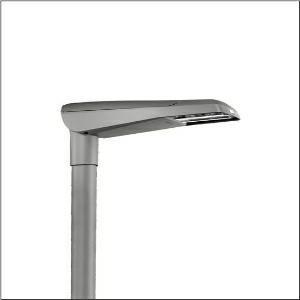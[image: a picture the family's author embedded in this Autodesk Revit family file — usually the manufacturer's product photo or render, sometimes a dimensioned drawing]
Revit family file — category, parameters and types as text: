
# Revit family: streetlight_sl_11_iq_micro___st0_5a_5xc1b41e08ce_6374
name_source: partatom
category: Lighting Fixtures
units: mm (PartAtom-declared; Revit-internal decimal feet)

## family parameters
Cut with Voids When Loaded = No
Host = Face
Light Source = No
Part Type = Normal
Room Calculation Point = No
Round Connector Dimension = Use Diameter
Shared = No

## types (1)
- --- (1 x LED, 1940 lm, 12.6 W, 4000K)
    Apparent Load = 13 VA
    CIE Flux Codes = 42 72 97 100 100
    Color Rendering = 70
    Color Temperature = 4000K
    Default Elevation = 1800 mm
    Description = Streetlight SL 11 iQ micro, mast luminaire, primary light control with 3 zone facetted reflector, of plastic, silver coated, highly specular, primary optical cover: cover, of PMMA, transparent, light distribution: ST0.5a, light emission: direct distribution, primary light characteristic: asymmetric, installation type: post-top, side-entry, lamps: LED, High Power LED, rated values: 1.940lm | 12,6W | 154lm/W (begin service life); end service life: 1.940lm | 12,9W; at 50% lumin. flux: 970lm | 6,8W | 142,6lm/W, colour temperature: 4000K, colour rendering: CRI > 70, light colour: 740, light setting 1 begin service life: 100% | 1.940lm | 12,6W | 154lm/W | 4.000K, light setting 1 end service life: 12,9W, further light settings possible, control: optimised constant luminous flux control (CLO 2.0), Desk-Remote (wireless, voltage-free reading and setting of iQ features in the workshop via application-optimized NFC function/RFID function), Light-Fading, Smart-Wire, Night-Set, Lumen-Switch, Temp-Guard, Auto-Match, with cable H07RN-F 3x 1.5mm², mains connection: 230..240V, AC, 50/60Hz, connection cable pre-assembled, cable length: 5,5m, luminaire housing, of diecast aluminium, powder-coated, SITECO metallic grey (DB 702S), please order mast flange separately, inclination adjustable without tools: 0°, 5°, 10°, 15° (post-top) | 0°, -5°, -10°, -15° (side-entry), sealing non-destructively replaceable, multi-level sealing system, length: 600mm, width: 174mm, height: 116mm, mast flange for spigot size: 42mm (side-entry): 5XC10008XM4, 60/48mm (side-entry/post-top): 5XC10108XM2, 76/60mm (side-entry/post-top): 5XC10108XM1, equipment: standard, protection rating (complete): IP66, insulation class (complete): insulation class II (safety insulation), certification: CE, ENEC, ENEC+, VDE, impact resistance: IK10, permissible operating ambient temperature for outdoor applications: -25..+50°C, standard-compliant lighting for roads and squares, Environmental Product Declaration (EPD) tested and certified by an independent institute, packaging unit: 1 piece

Light Distribution: ST0.5a
    Height = 116 mm
    Lamp = 1 x LED
    Lamp Light Flux = 1940 lm
    Lamp Power = 12.6 W
    Lamp count = 1
    Length = 600 mm
    Luminous efficacy = 154 lm/W
    Manufacturer = Siteco
    ModVariant = No
    Model = 5XC1B41E08CE
    Number of Poles = 1
    OnlyDefault = Yes
    Power Factor = 1
    Product Name = Streetlight SL 11 iQ micro | ST0.5a
    Product group = mast luminaire | pylon top
    ProductGroupID = 6100
    Protection Class = Protection class II
    Protection Degree = IP 66
    RLX_Detail_Level = 1
    RLX_Emergency_Light_Flux = 0 lm
    RLX_Emergency_Type = 0
    RLX_Emergency_Type_DB = No
    RlxData = <blob elided: 26761 chars, md5=430a5af7>
    Socket = socket
    Standby Power = 0 W
    System Light Flux = 1940 lm
    System Power = 13 W
    Type Comments = factory setting: luminous flux: 100 % | dim-lin: 254 | 229 mA
    Type Image = l_1006566.jpg
    URL = http://relux.com
    VarID = @adj_021853
    Voltage = 0 V
    Weight = 0.00 kg
    Width = 174 mm

## geometry (parser evidence)
native form markers: Blend x4, Sweep x12
no freeform markers — native parametric forms only
